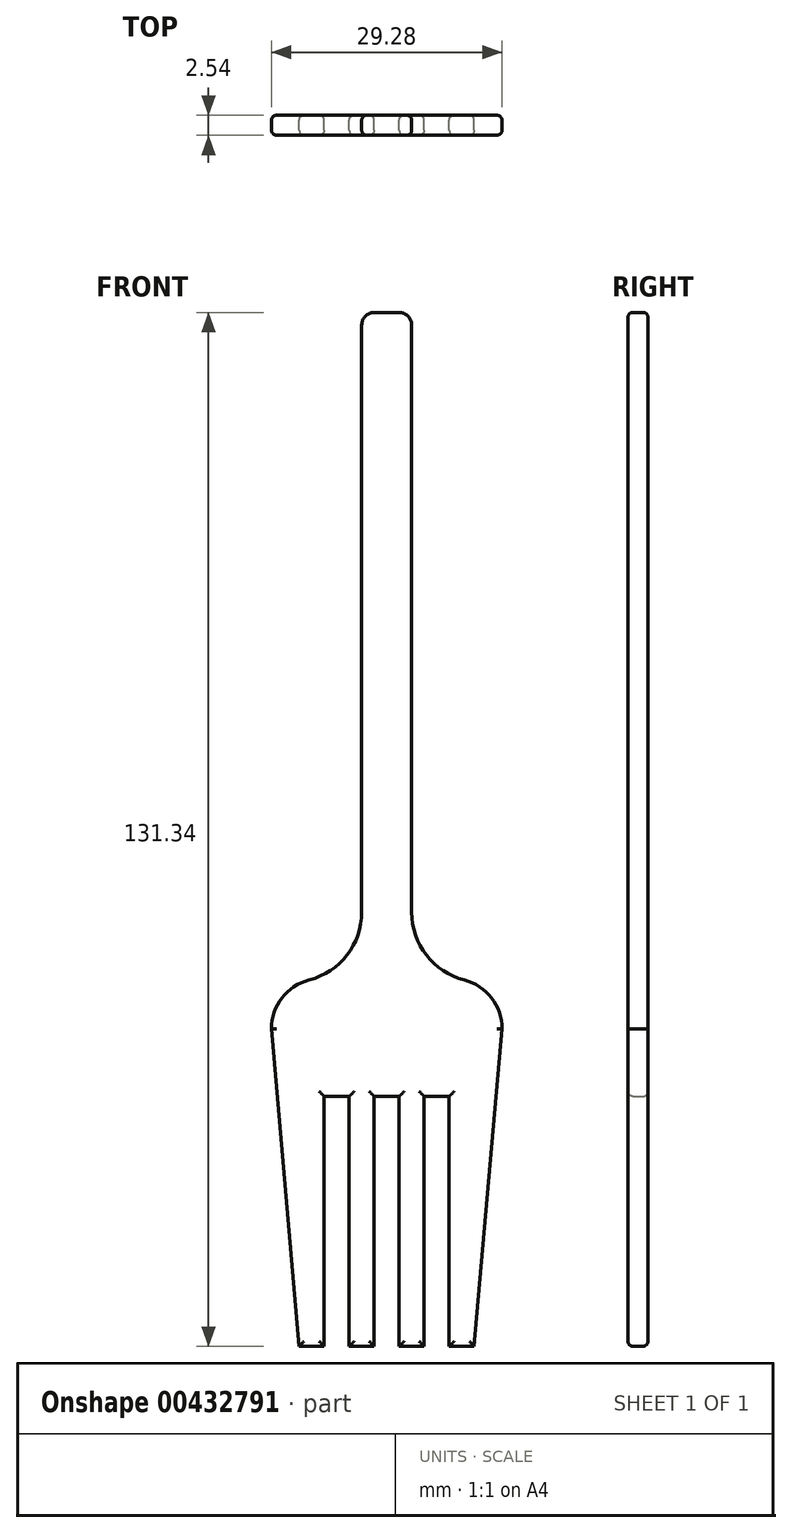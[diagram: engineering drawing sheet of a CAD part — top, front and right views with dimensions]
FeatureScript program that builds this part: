
annotation { "Feature Type Name" : "Feature", "Feature Type Description" : "" }
export const myFeature = defineFeature(function(context is Context, id is Id, definition is map)
    precondition{}
    {
        {
            var Q0;
            Q0=qCreatedBy(makeId("Front.planeOp"),FACE);
            var sketch = newSketch(context, id + "F0", { "sketchPlane" : qUnion([Q0])});
            skLineSegment(sketch, "E0.bottom", {"start": v(-3.18, 0) * mm, "end": v(3.18, 0) * mm});
            skLineSegment(sketch, "E0.top", {"start": v(-3.18, 74.61) * mm, "end": v(3.18, 74.61) * mm});
            skLineSegment(sketch, "E0.left", {"start": v(-3.17, 0) * mm, "end": v(-3.18, 74.61) * mm});
            skLineSegment(sketch, "E0.right", {"start": v(3.18, 0) * mm, "end": v(3.17, 74.61) * mm});
            skLineSegment(sketch, "E1", {"start": v(0, 0) * mm, "end": v(0, 83.46) * mm, "construction": true});
            skPoint(sketch, "E2", {"position": v(-1.59, 74.61) * mm});
            skArc(sketch, "E3", {"start": v(-3.18, 74.61) * mm, "mid": v(-2.71, 75.74) * mm, "end": v(-1.59, 76.2) * mm});
            skArc(sketch, "E4.MirrorCS", {"start": v(3.18, 74.61) * mm, "mid": v(2.71, 75.74) * mm, "end": v(1.59, 76.2) * mm});
            skLineSegment(sketch, "E5", {"start": v(-1.59, 76.2) * mm, "end": v(1.59, 76.2) * mm});
            skLineSegment(sketch, "E6.bottom", {"start": v(-4.76, -23.4) * mm, "end": v(-1.59, -23.4) * mm});
            skLineSegment(sketch, "E6.top", {"start": v(-4.76, -55.14) * mm, "end": v(-1.59, -55.14) * mm});
            skLineSegment(sketch, "E6.left", {"start": v(-4.76, -23.4) * mm, "end": v(-4.76, -55.14) * mm});
            skLineSegment(sketch, "E6.right", {"start": v(-1.59, -23.4) * mm, "end": v(-1.59, -55.14) * mm});
            skLineSegment(sketch, "E7", {"start": v(-7.94, -23.4) * mm, "end": v(-7.94, -55.14) * mm});
            skLineSegment(sketch, "E8", {"start": v(-7.94, -55.14) * mm, "end": v(-11.11, -55.14) * mm});
            skLineSegment(sketch, "E9", {"start": v(-11.11, -55.14) * mm, "end": v(-13.9, -23.4) * mm});
            skLineSegment(sketch, "E10", {"start": v(-13.9, -23.4) * mm, "end": v(-7.94, -23.4) * mm});
            skLineSegment(sketch, "E11", {"start": v(-7.94, -23.4) * mm, "end": v(-4.76, -23.4) * mm});
            skArc(sketch, "E12", {"start": v(-3.17, 0) * mm, "mid": v(-5.04, -5.45) * mm, "end": v(-9.86, -8.61) * mm});
            skArc(sketch, "E13", {"start": v(-9.86, -8.61) * mm, "mid": v(-13.33, -10.9) * mm, "end": v(-14.64, -14.83) * mm});
            skLineSegment(sketch, "E14", {"start": v(-14.64, -14.83) * mm, "end": v(-13.9, -23.4) * mm});
            skLineSegment(sketch, "E15.MirrorCS", {"start": v(7.94, -23.4) * mm, "end": v(4.76, -23.4) * mm});
            skLineSegment(sketch, "E16.MirrorCS", {"start": v(14.64, -14.83) * mm, "end": v(13.9, -23.4) * mm});
            skLineSegment(sketch, "E17.MirrorCS", {"start": v(4.76, -23.4) * mm, "end": v(4.76, -55.14) * mm});
            skLineSegment(sketch, "E18.MirrorCS", {"start": v(7.94, -55.14) * mm, "end": v(11.11, -55.14) * mm});
            skLineSegment(sketch, "E19.MirrorCS", {"start": v(7.94, -23.4) * mm, "end": v(7.94, -55.14) * mm});
            skLineSegment(sketch, "E20.MirrorCS", {"start": v(13.9, -23.4) * mm, "end": v(7.94, -23.4) * mm});
            skLineSegment(sketch, "E21.MirrorCS", {"start": v(11.11, -55.14) * mm, "end": v(13.9, -23.4) * mm});
            skLineSegment(sketch, "E22.MirrorCS", {"start": v(4.76, -55.14) * mm, "end": v(1.59, -55.14) * mm});
            skLineSegment(sketch, "E23.MirrorCS", {"start": v(4.76, -23.4) * mm, "end": v(1.59, -23.4) * mm});
            skLineSegment(sketch, "E24.MirrorCS", {"start": v(1.59, -23.4) * mm, "end": v(1.59, -55.14) * mm});
            skArc(sketch, "E25.MirrorCS", {"start": v(9.86, -8.61) * mm, "mid": v(13.33, -10.9) * mm, "end": v(14.64, -14.83) * mm});
            skArc(sketch, "E26.MirrorCS", {"start": v(3.17, 0) * mm, "mid": v(5.04, -5.45) * mm, "end": v(9.86, -8.61) * mm});
            skLineSegment(sketch, "E27", {"start": v(-1.59, -23.4) * mm, "end": v(1.59, -23.4) * mm});
            skSolve(sketch);
        }
        {
            var Q0;
            Q0 = qSketchRegion(id + "F0", true);
            extrude(context, id + "F1", {"entities" : qUnion([Q0]), "depth" : 2.54 * mm});
        }
        {
            var Q0;
            Q0=makeQuery(id+"F1.opExtrude","CAP_FACE",FACE,{"disambiguationData":[OSD([sQuery(id+"F0.wireOp",EDGE,"E0.left"),sQuery(id+"F0.wireOp",EDGE,"E0.right"),sQuery(id+"F0.wireOp",EDGE,"E3"),sQuery(id+"F0.wireOp",EDGE,"E4.MirrorCS"),sQuery(id+"F0.wireOp",EDGE,"E5"),sQuery(id+"F0.wireOp",EDGE,"E6.top"),sQuery(id+"F0.wireOp",EDGE,"E6.left"),sQuery(id+"F0.wireOp",EDGE,"E6.right"),sQuery(id+"F0.wireOp",EDGE,"E7"),sQuery(id+"F0.wireOp",EDGE,"E8"),sQuery(id+"F0.wireOp",EDGE,"E9"),sQuery(id+"F0.wireOp",EDGE,"E11"),sQuery(id+"F0.wireOp",EDGE,"E12"),sQuery(id+"F0.wireOp",EDGE,"E13"),sQuery(id+"F0.wireOp",EDGE,"E14"),sQuery(id+"F0.wireOp",EDGE,"E22.MirrorCS"),sQuery(id+"F0.wireOp",EDGE,"E21.MirrorCS"),sQuery(id+"F0.wireOp",EDGE,"E18.MirrorCS"),sQuery(id+"F0.wireOp",EDGE,"E16.MirrorCS"),sQuery(id+"F0.wireOp",EDGE,"E17.MirrorCS"),sQuery(id+"F0.wireOp",EDGE,"E24.MirrorCS"),sQuery(id+"F0.wireOp",EDGE,"E19.MirrorCS"),sQuery(id+"F0.wireOp",EDGE,"E15.MirrorCS"),sQuery(id+"F0.wireOp",EDGE,"E25.MirrorCS"),sQuery(id+"F0.wireOp",EDGE,"E26.MirrorCS"),sQuery(id+"F0.wireOp",EDGE,"E27")])],"isStart":false});
            var Q1;
            Q1=makeQuery(id+"F1.opExtrude","CAP_FACE",FACE,{"disambiguationData":[OSD([sQuery(id+"F0.wireOp",EDGE,"E0.left"),sQuery(id+"F0.wireOp",EDGE,"E0.right"),sQuery(id+"F0.wireOp",EDGE,"E3"),sQuery(id+"F0.wireOp",EDGE,"E4.MirrorCS"),sQuery(id+"F0.wireOp",EDGE,"E5"),sQuery(id+"F0.wireOp",EDGE,"E6.top"),sQuery(id+"F0.wireOp",EDGE,"E6.left"),sQuery(id+"F0.wireOp",EDGE,"E6.right"),sQuery(id+"F0.wireOp",EDGE,"E7"),sQuery(id+"F0.wireOp",EDGE,"E8"),sQuery(id+"F0.wireOp",EDGE,"E9"),sQuery(id+"F0.wireOp",EDGE,"E11"),sQuery(id+"F0.wireOp",EDGE,"E12"),sQuery(id+"F0.wireOp",EDGE,"E13"),sQuery(id+"F0.wireOp",EDGE,"E14"),sQuery(id+"F0.wireOp",EDGE,"E22.MirrorCS"),sQuery(id+"F0.wireOp",EDGE,"E21.MirrorCS"),sQuery(id+"F0.wireOp",EDGE,"E18.MirrorCS"),sQuery(id+"F0.wireOp",EDGE,"E16.MirrorCS"),sQuery(id+"F0.wireOp",EDGE,"E17.MirrorCS"),sQuery(id+"F0.wireOp",EDGE,"E24.MirrorCS"),sQuery(id+"F0.wireOp",EDGE,"E19.MirrorCS"),sQuery(id+"F0.wireOp",EDGE,"E15.MirrorCS"),sQuery(id+"F0.wireOp",EDGE,"E25.MirrorCS"),sQuery(id+"F0.wireOp",EDGE,"E26.MirrorCS"),sQuery(id+"F0.wireOp",EDGE,"E27")])],"isStart":true});
            fillet(context, id + "F2", {"entities" : qUnion([Q0, Q1]), "radius" : 0.64 * mm, "tangentPropagation" : true, "allowEdgeOverflow" : false});
        }
    });
